# Revit family: Sanitary_Napkin_Disposal-Bobrick-TrimLineSeries-B-35139
name_source: partatom
category: Specialty Equipment
revit_build: Autodesk Revit 2014 (Build: 20130308_1515(x64)
units: mm (PartAtom-declared; Revit-internal decimal feet)

## types (1)
- B-35139
    ADA Compliant = Yes
    Assembly Code = E1090900
    Default Elevation = 30"
    Description = TrimLineSeries™ Surface-Mounted Sanitary Napkin Disposal
    Height = 14 1/8"
    Installation Type = Surface-Mounted
    Length = 4 1/2"
    Manufacturer = Bobrick Washroom Equipment, Inc.
    Material = Stainless Steel-Bobrick-Type 304-Satin
    Model = B-35139
    Price = Prices may vary. Please consult Manufacturer Representative for most up-to-date price list.
    Product Page URL = http://www.bobrick.com
    Specification = Surface-mounted sanitary napkin disposal shall be Type-304 stainless steel with all-welded construction; exposed surfaces shall have satin finish. Door shall be Type-304, 20-gauge (0.9mm) stainless steel with satin-finish. Secured to cabinet with two rivets and equipped with a magnet catch and cable door-swing limiter. Waste receptacle shall be Type-304, heavy-gauge stainless steel. All-welded construction with a capacity of 0.6-gal. (2.3-L).
    URL = http://www.bobrick.com
    Warranty Information = 1 Year Limited Warranty
    Width = 8 1/16"

## geometry (parser evidence)
native form markers: Sweep x3
no freeform markers — native parametric forms only
